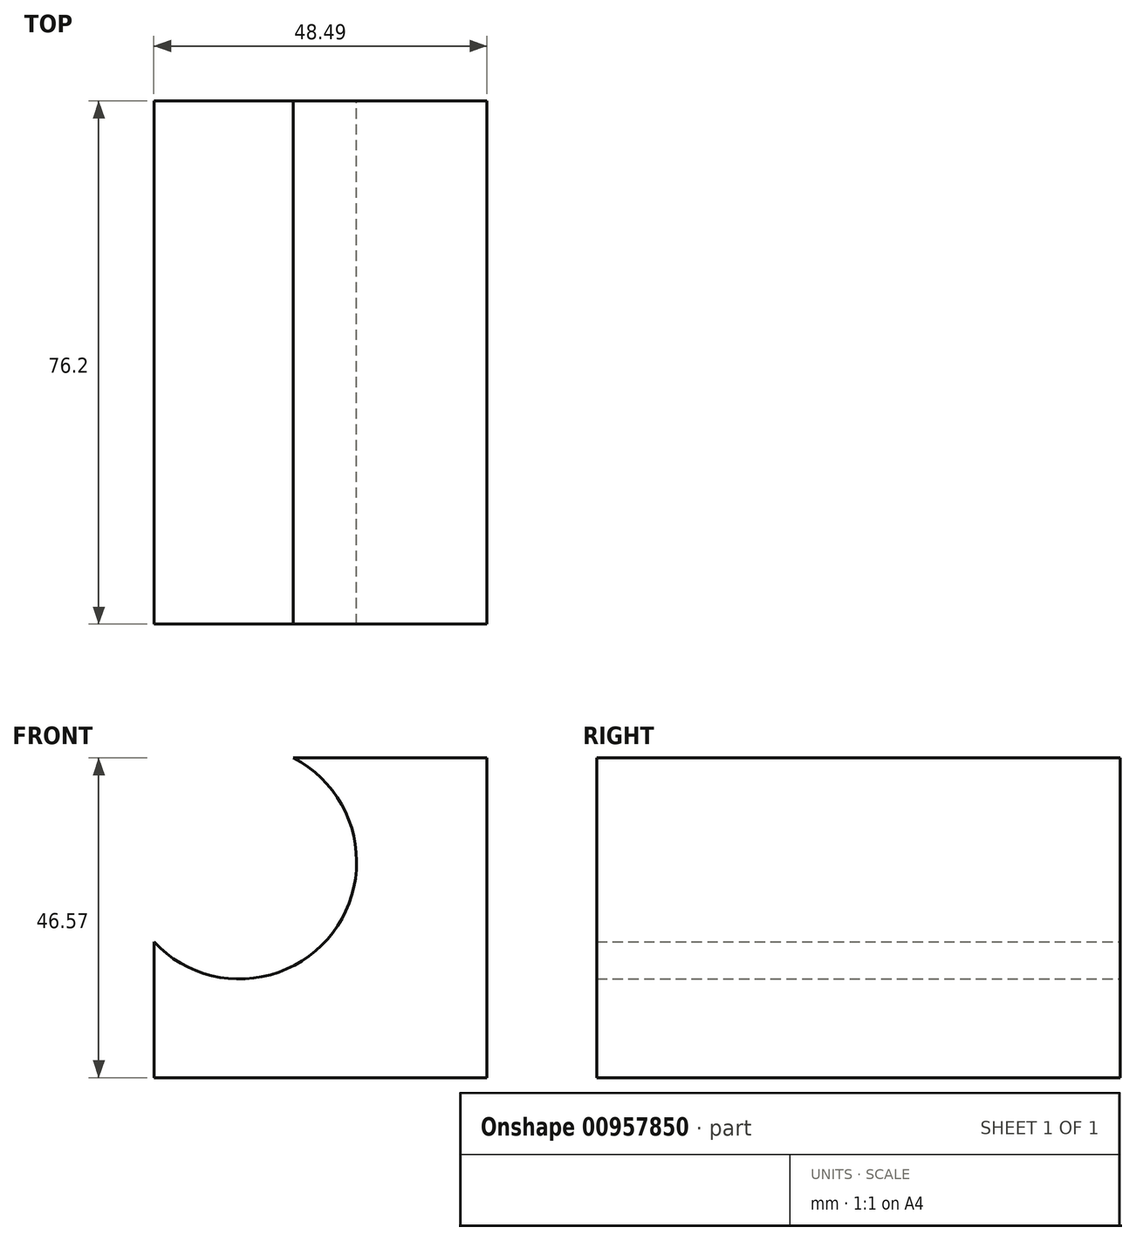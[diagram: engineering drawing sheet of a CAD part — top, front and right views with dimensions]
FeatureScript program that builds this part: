
annotation { "Feature Type Name" : "Feature", "Feature Type Description" : "" }
export const myFeature = defineFeature(function(context is Context, id is Id, definition is map)
    precondition{}
    {
        {
            var Q0;
            Q0=qCreatedBy(makeId("Front.planeOp"),FACE);
            var sketch = newSketch(context, id + "F0", { "sketchPlane" : qUnion([Q0])});
            skLineSegment(sketch, "E0.bottom", {"start": v(-21.18, 23.96) * mm, "end": v(27.3, 23.96) * mm});
            skLineSegment(sketch, "E0.top", {"start": v(-21.18, -22.61) * mm, "end": v(27.3, -22.61) * mm});
            skLineSegment(sketch, "E0.left", {"start": v(-21.18, 23.96) * mm, "end": v(-21.18, -22.61) * mm});
            skLineSegment(sketch, "E0.right", {"start": v(27.3, 23.96) * mm, "end": v(27.3, -22.61) * mm});
            skCircle(sketch, "E1", {"center": v(-8.72, 8.82) * mm, "radius": 17.06 * mm});
            skSolve(sketch);
        }
        {
            var Q0;
            {var subQ0=sQuery(id+"F0.wireOp",EDGE,"E0.left");var subQ1=sQuery(id+"F0.wireOp",EDGE,"E0.bottom");var subQ2=makeQuery(id+"F0.imprint","INTERSECT",VERTEX,{"derivedFrom":[subQ1,subQ0]});Q0=makeQuery(id+"F0.imprint","IMPRINT",FACE,{"disambiguationData":[TD([[makeQuery(id+"F0.imprint","IMPRINT",EDGE,{"disambiguationData":[TD([[subQ2,-1.0]])],"derivedFrom":subQ1}),-1.0]])]});}
            var Q1;
            {var subQ0=sQuery(id+"F0.wireOp",EDGE,"E1");var subQ1=sQuery(id+"F0.wireOp",EDGE,"E0.bottom");var subQ2=makeQuery(id+"F0.imprint","INTERSECT",VERTEX,{"disambiguationData":[OD(0.0)],"derivedFrom":[subQ1,subQ0]});Q1=makeQuery(id+"F0.imprint","IMPRINT",FACE,{"disambiguationData":[TD([[makeQuery(id+"F0.imprint","IMPRINT",EDGE,{"disambiguationData":[TD([[subQ2,-1.0]])],"derivedFrom":subQ1}),1.0]])]});}
            var Q2;
            {var subQ1=sQuery(id+"F0.wireOp",EDGE,"E0.top");Q2=makeQuery(id+"F0.imprint","IMPRINT",FACE,{"disambiguationData":[TD([[makeQuery(id+"F0.imprint","IMPRINT",EDGE,{"derivedFrom":subQ1}),1.0]])]});}
            extrude(context, id + "F1", {"entities" : qUnion([Q0, Q1, Q2]), "depth" : 76.2 * mm, "offsetDistance" : 25.4 * mm});
        }
        {
            var Q0;
            Q0=makeQuery(id+"F1.opExtrude","SWEPT_BODY",BODY,{"disambiguationData":[OSD([sQuery(id+"F0.wireOp",EDGE,"E0.bottom"),sQuery(id+"F0.wireOp",EDGE,"E1")])]});
            var Q1;
            Q1=makeQuery(id+"F1.opExtrude","SWEPT_BODY",BODY,{"disambiguationData":[OSD([sQuery(id+"F0.wireOp",EDGE,"E0.bottom"),sQuery(id+"F0.wireOp",EDGE,"E0.left"),sQuery(id+"F0.wireOp",EDGE,"E1")])]});
            deleteBodies(context, id + "F2", {"entities" : qUnion([Q0, Q1])});
        }
    });
